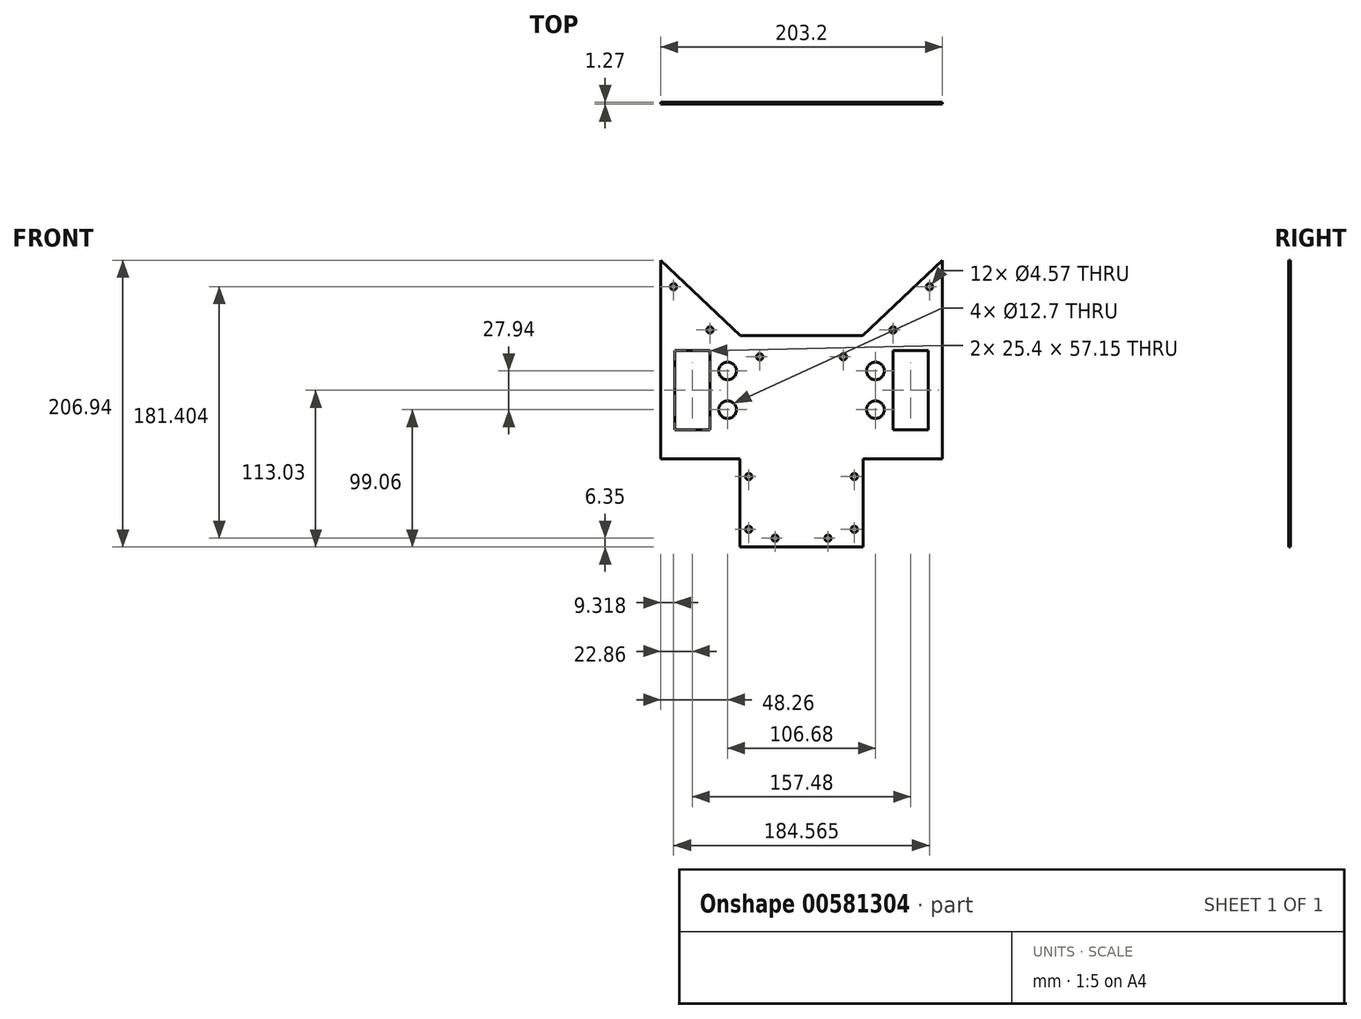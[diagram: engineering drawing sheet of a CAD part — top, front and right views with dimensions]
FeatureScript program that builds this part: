
annotation { "Feature Type Name" : "Feature", "Feature Type Description" : "" }
export const myFeature = defineFeature(function(context is Context, id is Id, definition is map)
    precondition{}
    {
        {
            var Q0;
            Q0=qCreatedBy(makeId("Front.planeOp"),FACE);
            var sketch = newSketch(context, id + "F0", { "sketchPlane" : qUnion([Q0])});
            skLineSegment(sketch, "E0.bottom", {"start": v(44.09, 76.2) * mm, "end": v(-44.09, 76.2) * mm});
            skLineSegment(sketch, "E0.top", {"start": v(44.45, -76.2) * mm, "end": v(-44.45, -76.2) * mm});
            skLineSegment(sketch, "E0.left", {"start": v(101.6, 76.2) * mm, "end": v(101.6, -12.7) * mm});
            skLineSegment(sketch, "E0.right", {"start": v(-101.6, 76.2) * mm, "end": v(-101.6, -12.7) * mm});
            skPoint(sketch, "E0.middle", {"position": v(0, 0) * mm});
            skLineSegment(sketch, "E1.bottom", {"start": v(-44.45, -76.2) * mm, "end": v(44.45, -76.2) * mm});
            skLineSegment(sketch, "E1.left", {"start": v(-44.45, -76.2) * mm, "end": v(-44.45, -12.7) * mm});
            skLineSegment(sketch, "E1.right", {"start": v(44.45, -76.2) * mm, "end": v(44.45, -12.7) * mm});
            skLineSegment(sketch, "E2", {"start": v(-44.45, -12.7) * mm, "end": v(-101.6, -12.7) * mm});
            skLineSegment(sketch, "E3", {"start": v(44.45, -12.7) * mm, "end": v(101.6, -12.7) * mm});
            skPoint(sketch, "E4.orphan", {"position": v(-101.6, -76.2) * mm});
            skLineSegment(sketch, "E5.bottom", {"start": v(-44.09, 76.2) * mm, "end": v(44.09, 76.2) * mm});
            skLineSegment(sketch, "E5.left", {"start": v(-101.6, 76.2) * mm, "end": v(-101.6, 50.8) * mm});
            skLineSegment(sketch, "E5.right", {"start": v(101.6, 76.2) * mm, "end": v(101.6, 50.8) * mm});
            skLineSegment(sketch, "E6.left", {"start": v(-91.44, 22.86) * mm, "end": v(-91.44, 50.8) * mm});
            skLineSegment(sketch, "E7.MirrorCS", {"start": v(91.44, 22.86) * mm, "end": v(91.44, 50.8) * mm});
            skLineSegment(sketch, "E8.top", {"start": v(-91.44, 65.4) * mm, "end": v(-66.04, 65.4) * mm});
            skLineSegment(sketch, "E8.left", {"start": v(-91.44, 50.8) * mm, "end": v(-91.44, 65.4) * mm});
            skLineSegment(sketch, "E8.right", {"start": v(-66.04, 50.8) * mm, "end": v(-66.04, 65.4) * mm});
            skLineSegment(sketch, "E9.top", {"start": v(-91.44, 8.25) * mm, "end": v(-66.04, 8.25) * mm});
            skLineSegment(sketch, "E9.left", {"start": v(-91.44, 22.86) * mm, "end": v(-91.44, 8.25) * mm});
            skLineSegment(sketch, "E9.right", {"start": v(-66.04, 22.86) * mm, "end": v(-66.04, 8.25) * mm});
            skLineSegment(sketch, "E10.MirrorCS", {"start": v(66.04, 50.8) * mm, "end": v(66.04, 65.4) * mm});
            skLineSegment(sketch, "E11.MirrorCS", {"start": v(91.44, 65.4) * mm, "end": v(66.04, 65.4) * mm});
            skLineSegment(sketch, "E12.MirrorCS", {"start": v(91.44, 50.8) * mm, "end": v(91.44, 65.4) * mm});
            skLineSegment(sketch, "E13.MirrorCS", {"start": v(91.44, 22.86) * mm, "end": v(91.44, 8.25) * mm});
            skLineSegment(sketch, "E14.MirrorCS", {"start": v(91.44, 8.25) * mm, "end": v(66.04, 8.25) * mm});
            skLineSegment(sketch, "E15.MirrorCS", {"start": v(66.04, 22.86) * mm, "end": v(66.04, 8.25) * mm});
            skLineSegment(sketch, "E16", {"start": v(-101.6, 76.2) * mm, "end": v(-101.6, 130.74) * mm});
            skLineSegment(sketch, "E17", {"start": v(-101.6, 130.74) * mm, "end": v(-44.09, 76.2) * mm});
            skLineSegment(sketch, "E18.MirrorCS", {"start": v(101.6, 130.74) * mm, "end": v(44.09, 76.2) * mm});
            skLineSegment(sketch, "E19.MirrorCS", {"start": v(101.6, 76.2) * mm, "end": v(101.6, 130.74) * mm});
            skCircle(sketch, "E20", {"center": v(-30.14, 61) * mm, "radius": 2.29 * mm});
            skCircle(sketch, "E21", {"center": v(-66.07, 80.42) * mm, "radius": 2.29 * mm});
            skCircle(sketch, "E22", {"center": v(-92.28, 111.55) * mm, "radius": 2.29 * mm});
            skCircle(sketch, "E23.MirrorC", {"center": v(30.14, 61) * mm, "radius": 2.29 * mm});
            skCircle(sketch, "E24.MirrorC", {"center": v(66.07, 80.42) * mm, "radius": 2.29 * mm});
            skCircle(sketch, "E25.MirrorC", {"center": v(92.28, 111.55) * mm, "radius": 2.29 * mm});
            skLineSegment(sketch, "E26", {"start": v(-66.04, 22.86) * mm, "end": v(-66.04, 50.8) * mm});
            skCircle(sketch, "E27", {"center": v(-53.34, 50.8) * mm, "radius": 6.35 * mm});
            skCircle(sketch, "E28", {"center": v(-53.34, 22.86) * mm, "radius": 6.35 * mm});
            skCircle(sketch, "E29.MirrorC", {"center": v(53.34, 50.8) * mm, "radius": 6.35 * mm});
            skCircle(sketch, "E30.MirrorC", {"center": v(53.34, 22.86) * mm, "radius": 6.35 * mm});
            skCircle(sketch, "E31", {"center": v(-38.1, -25.4) * mm, "radius": 2.29 * mm});
            skCircle(sketch, "E32", {"center": v(-38.1, -63.5) * mm, "radius": 2.29 * mm});
            skCircle(sketch, "E33", {"center": v(-19.05, -69.85) * mm, "radius": 2.29 * mm});
            skCircle(sketch, "E34.MirrorC", {"center": v(38.1, -25.4) * mm, "radius": 2.29 * mm});
            skCircle(sketch, "E35.MirrorC", {"center": v(38.1, -63.5) * mm, "radius": 2.29 * mm});
            skCircle(sketch, "E36.MirrorC", {"center": v(19.05, -69.85) * mm, "radius": 2.29 * mm});
            skLineSegment(sketch, "E37", {"start": v(66.04, 22.86) * mm, "end": v(66.04, 50.8) * mm});
            skSolve(sketch);
        }
        {
            var Q0;
            Q0 = qSketchRegion(id + "F0", true);
            extrude(context, id + "F1", {"entities" : qUnion([Q0]), "depth" : 1.27 * mm, "offsetDistance" : 25.4 * mm});
        }
    });
